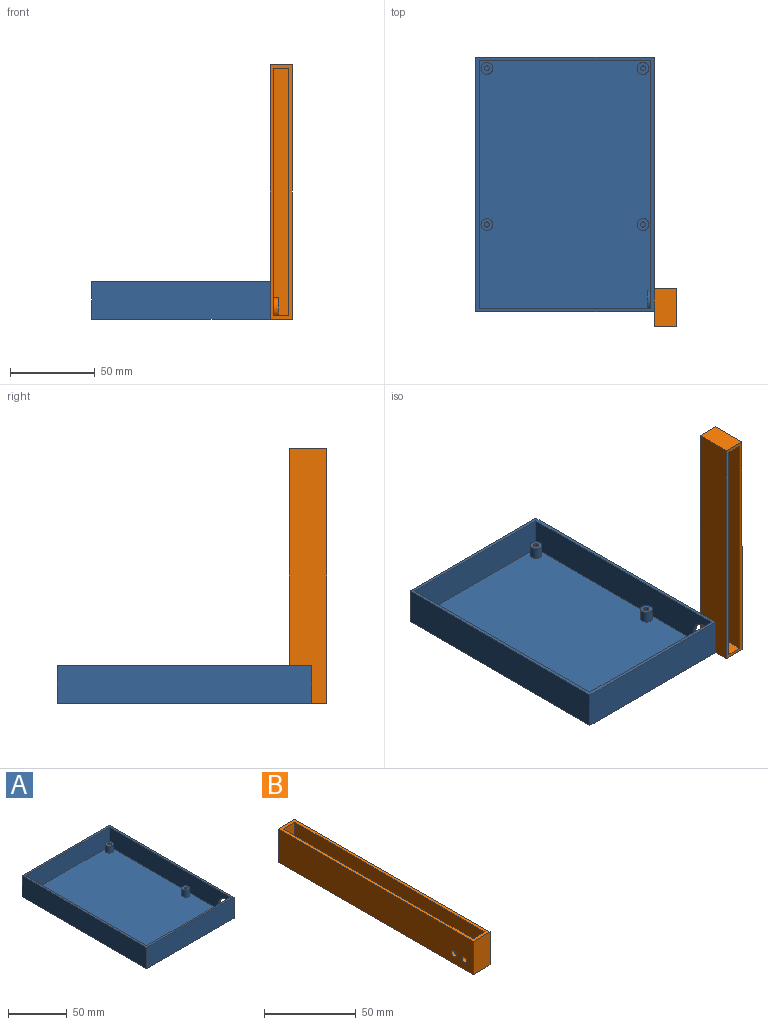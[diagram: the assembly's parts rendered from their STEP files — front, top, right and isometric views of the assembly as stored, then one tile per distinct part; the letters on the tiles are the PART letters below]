
ASSEMBLY  parts=2 mates=1
PART A: 36 faces, bbox 105x150x22 mm
  f0: plane 146x20mm, normal (-1,0,0), area 2753.3mm2, adj f3,f8,f9,f11,f30,f32,f33,f34
  f1: plane 150x22mm, normal (1,0,0), area 3223.7mm2, adj f5,f6,f9,f10,f28,f32,f33,f34
  f2: plane 0.87x0.86mm, normal (-1,0,0), area 0.3mm2, adj f3,f11,f29
  f3: plane 101x20mm, normal (0,1,0), area 2005mm2, adj f0,f2,f4,f9,f11,f29,f30,f31
  f4: plane 146x20mm, normal (1,0,0), area 2920mm2, adj f3,f8,f9,f11
  f5: plane 105x22mm, normal (0,-1,0), area 2310mm2, adj f1,f7,f9,f10
  f6: plane 105x22mm, normal (0,1,0), area 2310mm2, adj f1,f7,f9,f10
  f7: plane 150x22mm, normal (-1,0,0), area 3300mm2, adj f5,f6,f9,f10
  f8: plane 101x20mm, normal (0,-1,0), area 2020mm2, adj f0,f4,f9,f11
  f9: plane 150x105mm, normal (0,0,1), area 1004mm2, adj f0,f1,f3,f4,f5,f6,f7,f8
  f10: plane 150x105mm, normal (0,0,-1), area 15750mm2, adj f1,f5,f6,f7
  f11: plane 146x101mm, normal (0,0,1), area 14576.8mm2, adj f0,f2,f3,f4,f8,f13,f17,f21
  f12: cylinder r=1.5mm len=7mm, axis (0,0,-1), area 66mm2, adj f14,f15
  f13: cylinder r=3.5mm len=7mm, axis (0,0,-1), area 153.9mm2, adj f11,f14
  f14: plane 7x7mm, normal (0,0,1), area 31.4mm2, adj f12,f13
  f15: plane 3x3mm, normal (0,0,1), area 7.1mm2, adj f12
  f16: cylinder r=1.5mm len=7mm, axis (0,0,-1), area 66mm2, adj f18,f19
  f17: cylinder r=3.5mm len=7mm, axis (0,0,-1), area 153.9mm2, adj f11,f18
  f18: plane 7x7mm, normal (0,0,1), area 31.4mm2, adj f16,f17
  f19: plane 3x3mm, normal (0,0,1), area 7.1mm2, adj f16
  f20: cylinder r=1.5mm len=7mm, axis (0,0,-1), area 66mm2, adj f22,f23
  f21: cylinder r=3.5mm len=7mm, axis (0,0,-1), area 153.9mm2, adj f11,f22
  f22: plane 7x7mm, normal (0,0,1), area 31.4mm2, adj f20,f21
  f23: plane 3x3mm, normal (0,0,1), area 7.1mm2, adj f20
  f24: cylinder r=1.5mm len=7mm, axis (0,0,-1), area 66mm2, adj f26,f27
  f25: cylinder r=3.5mm len=7mm, axis (0,0,-1), area 153.9mm2, adj f11,f26
  f26: plane 7x7mm, normal (0,0,1), area 31.4mm2, adj f24,f25
  f27: plane 3x3mm, normal (0,0,1), area 7.1mm2, adj f24
  f28: cylinder r=1.7mm len=4mm, axis (1,0,0), area 42.7mm2, adj f1,f31
  f29: cylinder r=6mm len=2mm, axis (1,0,0), area 2.4mm2, adj f2,f3,f11,f31
  f30: cylinder r=6mm len=10.68mm, axis (1,0,0), area 40.1mm2, adj f0,f3,f11,f31
  f31: plane 10.68x10.62mm, normal (-1,0,0), area 90.1mm2, adj f3,f11,f28,f29,f30
  f32: extruded ~10.14x10.11mm, area 32.5mm2, adj f0,f1,f33,f35
  f33: cylinder r=2mm len=4mm, axis (1,0,0), area 12.6mm2, adj f0,f1,f32,f34
  f34: extruded ~6.14x6.1mm, area 19.2mm2, adj f0,f1,f33,f35
  f35: cylinder r=2mm len=4mm, axis (1,0,0), area 12.6mm2, adj f0,f1,f32,f34
PART B: 17 faces, bbox 13x150x22 mm
  f0: plane 20x9mm, normal (0,1,0), area 157.5mm2, adj f1,f2,f6,f8,f10,f14,f15,f16
  f1: plane 0.87x0.86mm, normal (1,0,0), area 0.3mm2, adj f0,f2,f16
  f2: plane 146x9mm, normal (0,0,1), area 1291.1mm2, adj f0,f1,f6,f7,f8,f14,f15,f16
  f3: plane 22x13mm, normal (0,1,0), area 286mm2, adj f4,f9,f10,f11
  f4: plane 150x22mm, normal (-1,0,0), area 3278.4mm2, adj f3,f5,f10,f11,f12,f13
  f5: plane 22x13mm, normal (0,-1,0), area 286mm2, adj f4,f9,f10,f11
  f6: plane 146x20mm, normal (1,0,0), area 2808mm2, adj f0,f2,f7,f10,f12,f14
  f7: plane 20x9mm, normal (0,-1,0), area 180mm2, adj f2,f6,f8,f10
  f8: plane 146x20mm, normal (-1,0,0), area 2920mm2, adj f0,f2,f7,f10
  f9: plane 150x22mm, normal (1,0,0), area 3300mm2, adj f3,f5,f10,f11
  f10: plane 150x13mm, normal (0,0,1), area 636mm2, adj f0,f3,f4,f5,f6,f7,f8,f9
  f11: plane 150x13mm, normal (0,0,-1), area 1950mm2, adj f3,f4,f5,f9
  f12: cylinder r=2mm len=4mm, axis (-1,0,0), area 25.1mm2, adj f4,f6
  f13: cylinder r=1.7mm len=5mm, axis (-1,0,0), area 53.4mm2, adj f4,f15
  f14: cylinder r=6mm len=10.68mm, axis (-1,0,0), area 60.2mm2, adj f0,f2,f6,f15
  f15: plane 10.68x10.62mm, normal (1,0,0), area 90.1mm2, adj f0,f2,f13,f14,f16
  f16: cylinder r=6mm len=3mm, axis (-1,0,0), area 3.7mm2, adj f0,f1,f2,f15
PLACE A at identity fixed
PLACE B rot(axis=(1,0,0),90deg) t=(0,-61.7,74.94)mm
MATE revolute A.f28 <-> B.f14  axis (1,0,0) through (52.5,-68.32,6.62)mm
